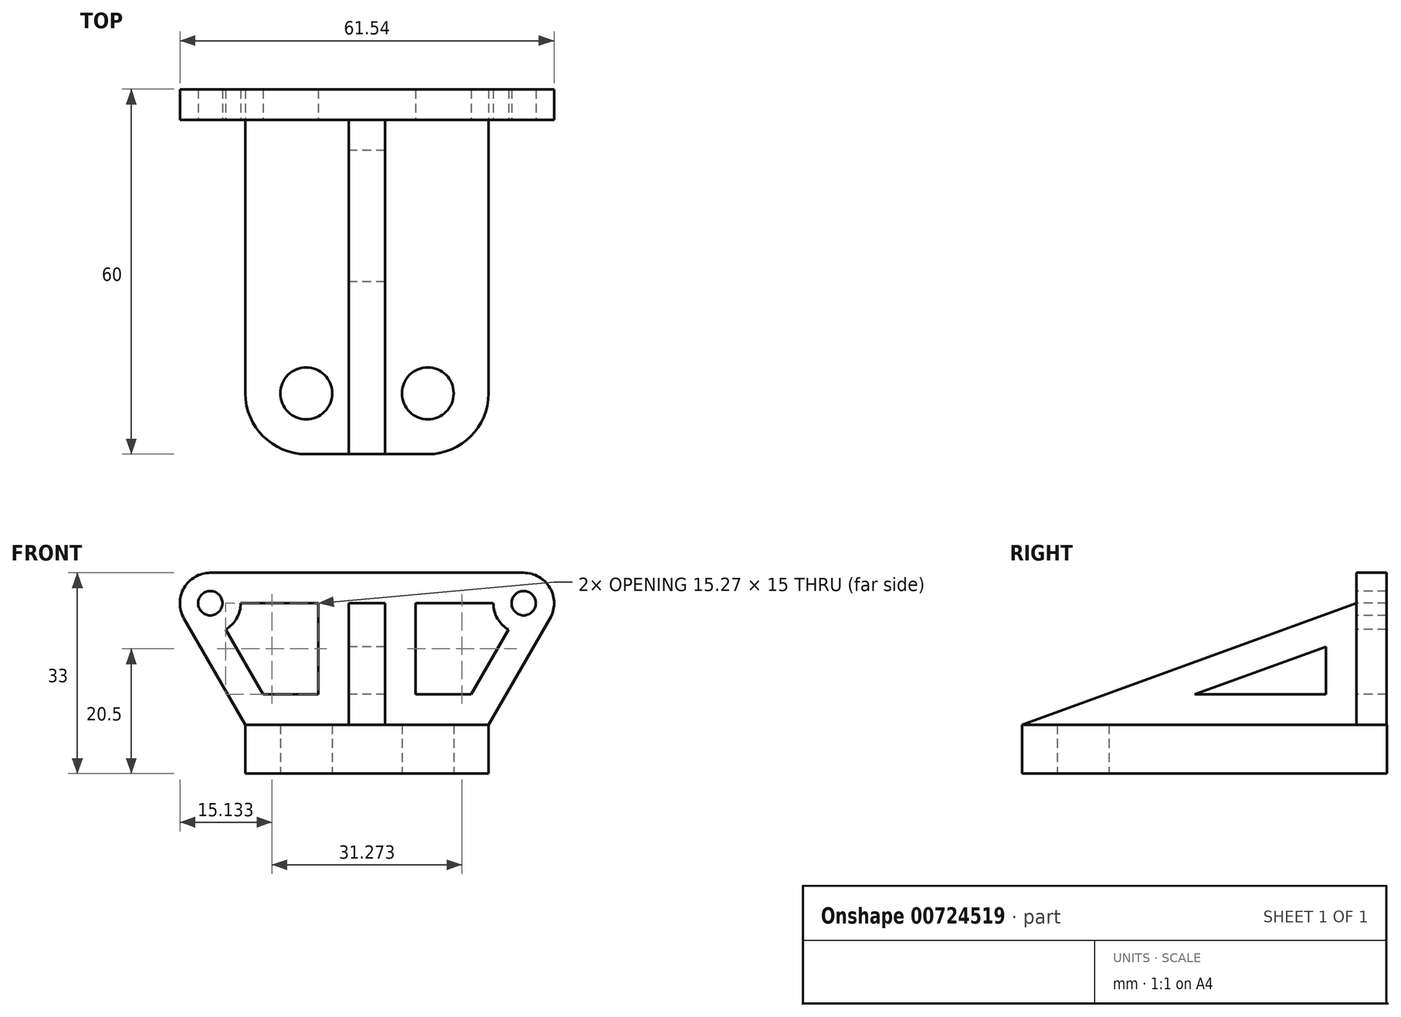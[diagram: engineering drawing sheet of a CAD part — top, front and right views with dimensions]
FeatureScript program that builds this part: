
annotation { "Feature Type Name" : "Feature", "Feature Type Description" : "" }
export const myFeature = defineFeature(function(context is Context, id is Id, definition is map)
    precondition{}
    {
        {
            var Q0;
            Q0=qCreatedBy(makeId("Top.planeOp"),FACE);
            var sketch = newSketch(context, id + "F0", { "sketchPlane" : qUnion([Q0])});
            skLineSegment(sketch, "E0", {"start": v(-20, 26.29) * mm, "end": v(-20, -23.71) * mm});
            skLineSegment(sketch, "E1", {"start": v(-10, -33.71) * mm, "end": v(10, -33.71) * mm});
            skLineSegment(sketch, "E2", {"start": v(20, 26.29) * mm, "end": v(20, -23.71) * mm});
            skLineSegment(sketch, "E3", {"start": v(-20, 26.29) * mm, "end": v(20, 26.29) * mm});
            skPoint(sketch, "E4.visualSharp", {"position": v(-20, -33.71) * mm});
            skArc(sketch, "E4.filletArc", {"start": v(-20, -23.71) * mm, "mid": v(-17.07, -30.78) * mm, "end": v(-10, -33.71) * mm});
            skPoint(sketch, "E5.visualSharp", {"position": v(20, -33.71) * mm});
            skArc(sketch, "E5.filletArc", {"start": v(10, -33.71) * mm, "mid": v(17.07, -30.78) * mm, "end": v(20, -23.71) * mm});
            skCircle(sketch, "E6", {"center": v(-10, -23.71) * mm, "radius": 4.27 * mm});
            skLineSegment(sketch, "E7", {"start": v(0, 26.29) * mm, "end": v(0, -33.71) * mm, "construction": true});
            skCircle(sketch, "E8.MirrorC", {"center": v(10, -23.71) * mm, "radius": 4.27 * mm});
            skSolve(sketch);
        }
        {
            var Q0;
            Q0=qSketchRegion(id+"F0",true);
            extrude(context, id + "F1", {"entities" : qUnion([Q0]), "depth" : 8 * mm});
        }
        {
            var Q0;
            Q0=qCreatedBy(makeId("Right.planeOp"),FACE);
            var sketch = newSketch(context, id + "F2", { "sketchPlane" : qUnion([Q0])});
            skLineSegment(sketch, "E9", {"start": v(-33.71, 8) * mm, "end": v(21.24, 28) * mm});
            skLineSegment(sketch, "E10", {"start": v(21.24, 28) * mm, "end": v(21.24, 8) * mm});
            skLineSegment(sketch, "E11", {"start": v(21.24, 8) * mm, "end": v(-33.71, 8) * mm});
            skLineSegment(sketch, "E12.0", {"start": v(-5.36, 13) * mm, "end": v(16.24, 20.86) * mm});
            skLineSegment(sketch, "E12.1", {"start": v(16.24, 13) * mm, "end": v(-5.36, 13) * mm});
            skLineSegment(sketch, "E12.2", {"start": v(16.24, 20.86) * mm, "end": v(16.24, 13) * mm});
            skSolve(sketch);
        }
        {
            var Q0;
            Q0=makeQuery(id+"F2.imprint","IMPRINT",FACE,{"disambiguationData":[TD([[makeQuery(id+"F2.imprint","IMPRINT",EDGE,{"derivedFrom":sQuery(id+"F2.wireOp",EDGE,"E9")}),-1.0]])]});
            extrude(context, id + "F3", {"entities" : qUnion([Q0]), "operationType" : NewBodyOperationType.ADD, "endBound" : BoundingType.SYMMETRIC, "depth" : 6 * mm});
        }
        {
            var Q0;
            Q0=makeQuery(id+"F3.opExtrude","SWEPT_FACE",FACE,{"disambiguationData":[OSD([sQuery(id+"F2.wireOp",EDGE,"E10")])]});
            var sketch = newSketch(context, id + "F4", { "sketchPlane" : qUnion([Q0])});
            skLineSegment(sketch, "E13", {"start": v(-20, 8) * mm, "end": v(20, 8) * mm});
            skLineSegment(sketch, "E14", {"start": v(-20, 8) * mm, "end": v(-30.1, 25.5) * mm});
            skLineSegment(sketch, "E15", {"start": v(0, 28) * mm, "end": v(0, 8) * mm, "construction": true});
            skCircle(sketch, "E16", {"center": v(-25.77, 28) * mm, "radius": 5 * mm});
            skCircle(sketch, "E17", {"center": v(-25.77, 28) * mm, "radius": 2 * mm});
            skLineSegment(sketch, "E18", {"start": v(-25.77, 33) * mm, "end": v(0, 33) * mm});
            skLineSegment(sketch, "E19", {"start": v(-23.27, 23.67) * mm, "end": v(-17.11, 13) * mm});
            skLineSegment(sketch, "E20", {"start": v(-17.11, 13) * mm, "end": v(-8, 13) * mm});
            skLineSegment(sketch, "E21", {"start": v(-8, 13) * mm, "end": v(-8, 28) * mm});
            skLineSegment(sketch, "E22", {"start": v(-8, 28) * mm, "end": v(-20.77, 28) * mm});
            skLineSegment(sketch, "E23.MirrorCS", {"start": v(25.77, 33) * mm, "end": v(0, 33) * mm});
            skLineSegment(sketch, "E24.MirrorCS", {"start": v(8, 28) * mm, "end": v(20.77, 28) * mm});
            skLineSegment(sketch, "E25.MirrorCS", {"start": v(8, 13) * mm, "end": v(8, 28) * mm});
            skLineSegment(sketch, "E26.MirrorCS", {"start": v(17.11, 13) * mm, "end": v(8, 13) * mm});
            skLineSegment(sketch, "E27.MirrorCS", {"start": v(23.27, 23.67) * mm, "end": v(17.11, 13) * mm});
            skCircle(sketch, "E28.MirrorC", {"center": v(25.77, 28) * mm, "radius": 5 * mm});
            skCircle(sketch, "E29.MirrorC", {"center": v(25.77, 28) * mm, "radius": 2 * mm});
            skLineSegment(sketch, "E30.MirrorCS", {"start": v(20, 8) * mm, "end": v(30.1, 25.5) * mm});
            skSolve(sketch);
        }
        {
            var Q0;
            Q0=qSketchRegion(id+"F4",true);
            extrude(context, id + "F5", {"entities" : qUnion([Q0]), "operationType" : NewBodyOperationType.ADD, "depth" : 5 * mm});
        }
    });
